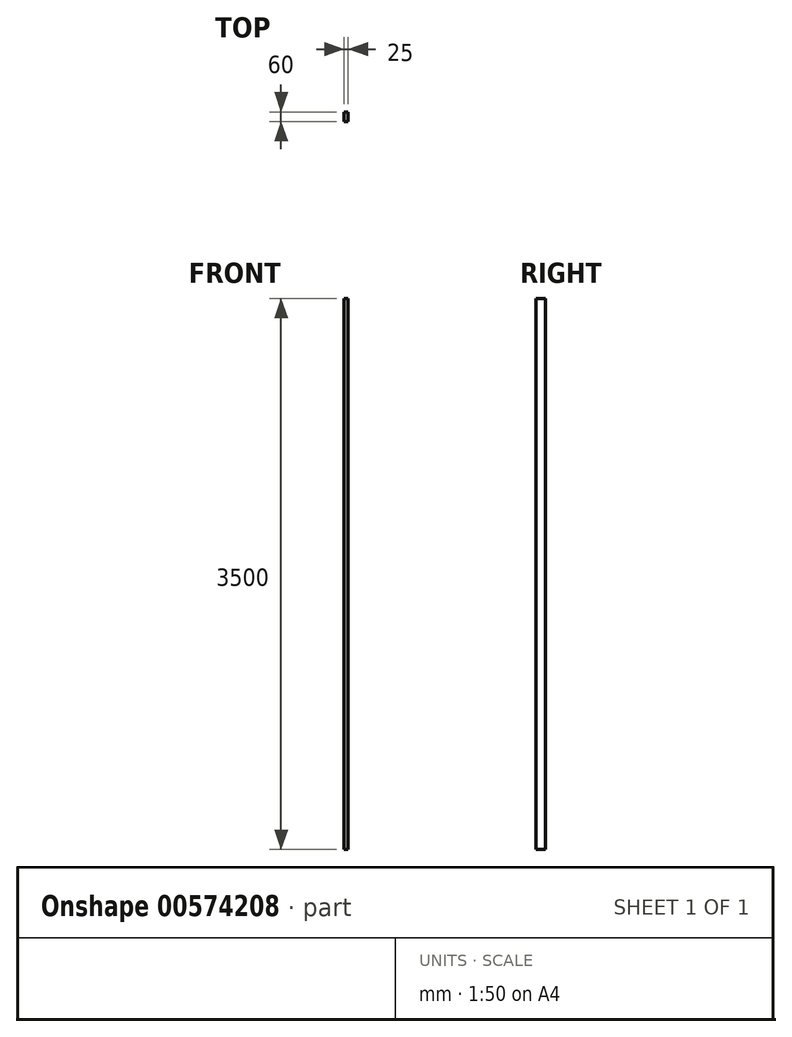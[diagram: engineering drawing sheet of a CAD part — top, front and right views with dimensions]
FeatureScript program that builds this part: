
annotation { "Feature Type Name" : "Feature", "Feature Type Description" : "" }
export const myFeature = defineFeature(function(context is Context, id is Id, definition is map)
    precondition{}
    {
        {
            var Q0;
            Q0=qCreatedBy(makeId("Top.planeOp"),FACE);
            var sketch = newSketch(context, id + "F0", { "sketchPlane" : qUnion([Q0])});
            skLineSegment(sketch, "E0.bottom", {"start": v(0, 0) * mm, "end": v(-25, 0) * mm});
            skLineSegment(sketch, "E0.top", {"start": v(0, 60) * mm, "end": v(-25, 60) * mm});
            skLineSegment(sketch, "E0.left", {"start": v(0, 0) * mm, "end": v(0, 60) * mm});
            skLineSegment(sketch, "E0.right", {"start": v(-25, 0) * mm, "end": v(-25, 60) * mm});
            skSolve(sketch);
        }
        {
            var Q0;
            Q0=makeQuery(id+"F0.imprint","IMPRINT",FACE,{"disambiguationData":[TD([[makeQuery(id+"F0.imprint","IMPRINT",EDGE,{"derivedFrom":sQuery(id+"F0.wireOp",EDGE,"E0.bottom")}),-1.0]])]});
            extrude(context, id + "F1", {"entities" : qUnion([Q0]), "oppositeDirection" : true, "depth" : 3500 * mm, "offsetDistance" : 25 * mm});
        }
    });
